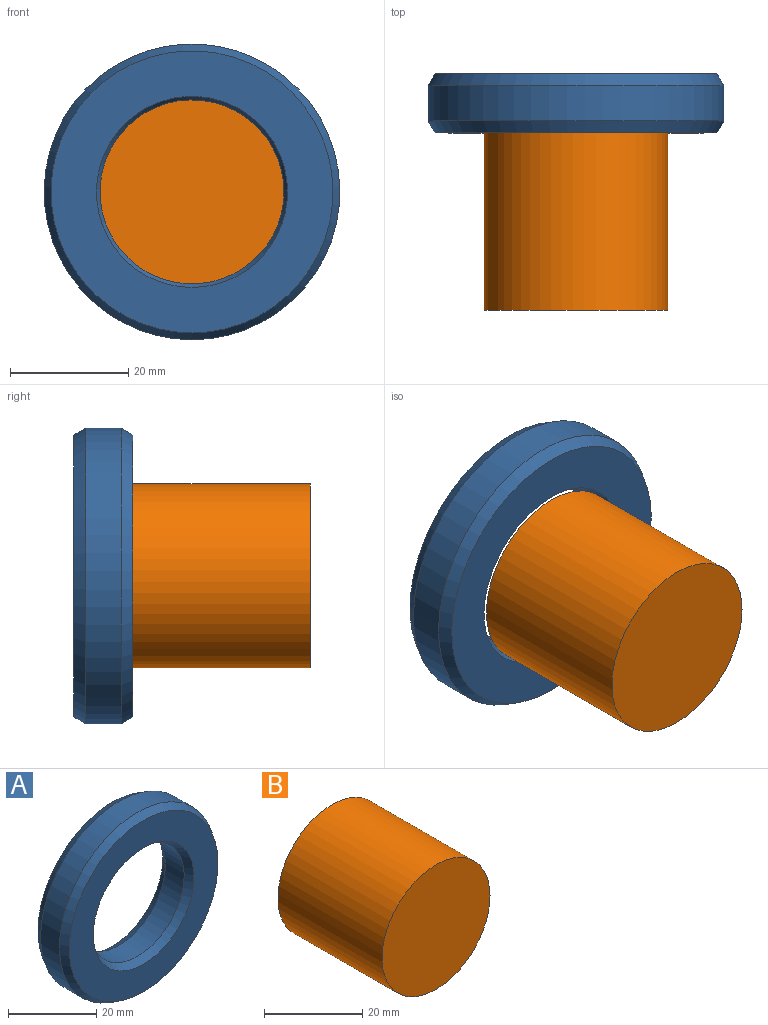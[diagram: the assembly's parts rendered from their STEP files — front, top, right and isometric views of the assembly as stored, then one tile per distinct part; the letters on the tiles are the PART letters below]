
ASSEMBLY  parts=2 mates=1
PART A: 8 faces, bbox 50x10x50 mm
  f0: cylinder r=15mm len=30mm, axis (0,1,0), area 565.5mm2, adj f4,f6
  f1: cylinder r=25mm len=50mm, axis (0,1,0), area 942.5mm2, adj f5,f7
  f2: plane 47.69x47.69mm, normal (0,-1,0), area 966.4mm2, adj f4,f5
  f3: plane 47.69x47.69mm, normal (0,1,0), area 966.4mm2, adj f6,f7
  f4: cone r=15mm half-angle=30deg, axis (0,-1,0), area 226mm2, adj f0,f2
  f5: cone r=23.85mm half-angle=30deg, axis (0,1,0), area 354.4mm2, adj f1,f2
  f6: cone r=16.15mm half-angle=30deg, axis (0,1,0), area 226mm2, adj f0,f3
  f7: cone r=25mm half-angle=30deg, axis (0,-1,0), area 354.4mm2, adj f1,f3
PART B: 3 faces, bbox 31.1x30x31.1 mm
  f0: cylinder r=15.55mm len=31.1mm, axis (0,1,0), area 2931.5mm2, adj f1,f2
  f1: plane 31.1x31.1mm, normal (0,-1,0), area 759.8mm2, adj f0
  f2: plane 31.1x31.1mm, normal (0,1,0), area 759.8mm2, adj f0
PLACE A at identity
PLACE B rot(axis=(1,0,0),180deg) t=(-44.92,-40,41.25)mm
MATE revolute B.f0 <-> A.f0  axis (0,1,0) through (0,-10,0)mm
